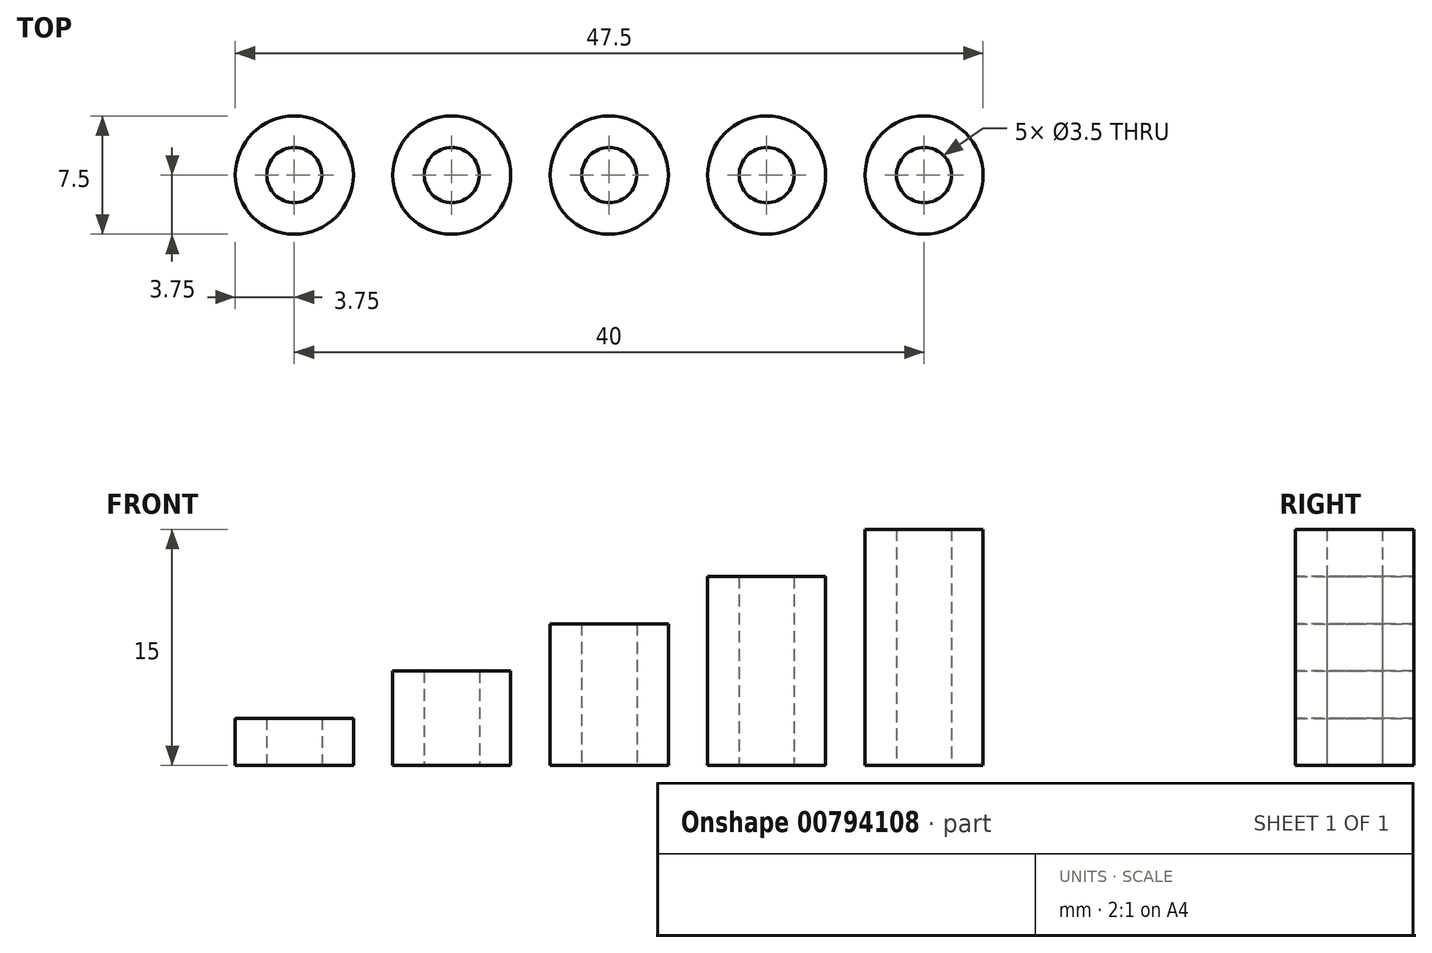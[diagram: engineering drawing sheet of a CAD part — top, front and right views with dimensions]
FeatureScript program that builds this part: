
annotation { "Feature Type Name" : "Feature", "Feature Type Description" : "" }
export const myFeature = defineFeature(function(context is Context, id is Id, definition is map)
    precondition{}
    {
        {
            var Q0;
            Q0=qCreatedBy(makeId("Top.planeOp"),FACE);
            var sketch = newSketch(context, id + "F0", { "sketchPlane" : qUnion([Q0])});
            skCircle(sketch, "E0", {"center": v(0, 0) * mm, "radius": 1.75 * mm});
            skCircle(sketch, "E1.0", {"center": v(0, 0) * mm, "radius": 3.75 * mm});
            skCircle(sketch, "E2.1.0.0", {"center": v(10, 0) * mm, "radius": 3.75 * mm});
            skCircle(sketch, "E2.1.0.1", {"center": v(10, 0) * mm, "radius": 1.75 * mm});
            skCircle(sketch, "E2.2.0.0", {"center": v(20, 0) * mm, "radius": 3.75 * mm});
            skCircle(sketch, "E2.2.0.1", {"center": v(20, 0) * mm, "radius": 1.75 * mm});
            skCircle(sketch, "E2.3.0.0", {"center": v(30, 0) * mm, "radius": 3.75 * mm});
            skCircle(sketch, "E2.3.0.1", {"center": v(30, 0) * mm, "radius": 1.75 * mm});
            skCircle(sketch, "E2.4.0.0", {"center": v(40, 0) * mm, "radius": 3.75 * mm});
            skCircle(sketch, "E2.4.0.1", {"center": v(40, 0) * mm, "radius": 1.75 * mm});
            skLineSegment(sketch, "E2.direction1", {"start": v(0, 0) * mm, "end": v(10, 0) * mm, "construction": true});
            skSolve(sketch);
        }
        {
            var Q0;
            Q0=makeQuery(id+"F0.imprint","IMPRINT",FACE,{"disambiguationData":[TD([[makeQuery(id+"F0.imprint","IMPRINT",EDGE,{"derivedFrom":sQuery(id+"F0.wireOp",EDGE,"E0")}),-1.0]])]});
            extrude(context, id + "F1", {"entities" : qUnion([Q0]), "depth" : 3 * mm, "offsetDistance" : 25 * mm});
        }
        {
            var Q0;
            Q0=makeQuery(id+"F0.imprint","IMPRINT",FACE,{"disambiguationData":[TD([[makeQuery(id+"F0.imprint","IMPRINT",EDGE,{"derivedFrom":sQuery(id+"F0.wireOp",EDGE,"E2.1.0.0")}),1.0]])]});
            extrude(context, id + "F2", {"entities" : qUnion([Q0]), "depth" : 6 * mm, "offsetDistance" : 25 * mm});
        }
        {
            var Q0;
            Q0=makeQuery(id+"F0.imprint","IMPRINT",FACE,{"disambiguationData":[TD([[makeQuery(id+"F0.imprint","IMPRINT",EDGE,{"derivedFrom":sQuery(id+"F0.wireOp",EDGE,"E2.2.0.0")}),1.0]])]});
            extrude(context, id + "F3", {"entities" : qUnion([Q0]), "depth" : 9 * mm, "offsetDistance" : 25 * mm});
        }
        {
            var Q0;
            Q0=makeQuery(id+"F0.imprint","IMPRINT",FACE,{"disambiguationData":[TD([[makeQuery(id+"F0.imprint","IMPRINT",EDGE,{"derivedFrom":sQuery(id+"F0.wireOp",EDGE,"E2.3.0.0")}),1.0]])]});
            extrude(context, id + "F4", {"entities" : qUnion([Q0]), "depth" : 12 * mm, "offsetDistance" : 25 * mm});
        }
        {
            var Q0;
            Q0=makeQuery(id+"F0.imprint","IMPRINT",FACE,{"disambiguationData":[TD([[makeQuery(id+"F0.imprint","IMPRINT",EDGE,{"derivedFrom":sQuery(id+"F0.wireOp",EDGE,"E2.4.0.0")}),1.0]])]});
            extrude(context, id + "F5", {"entities" : qUnion([Q0]), "depth" : 15 * mm, "offsetDistance" : 25 * mm});
        }
    });
